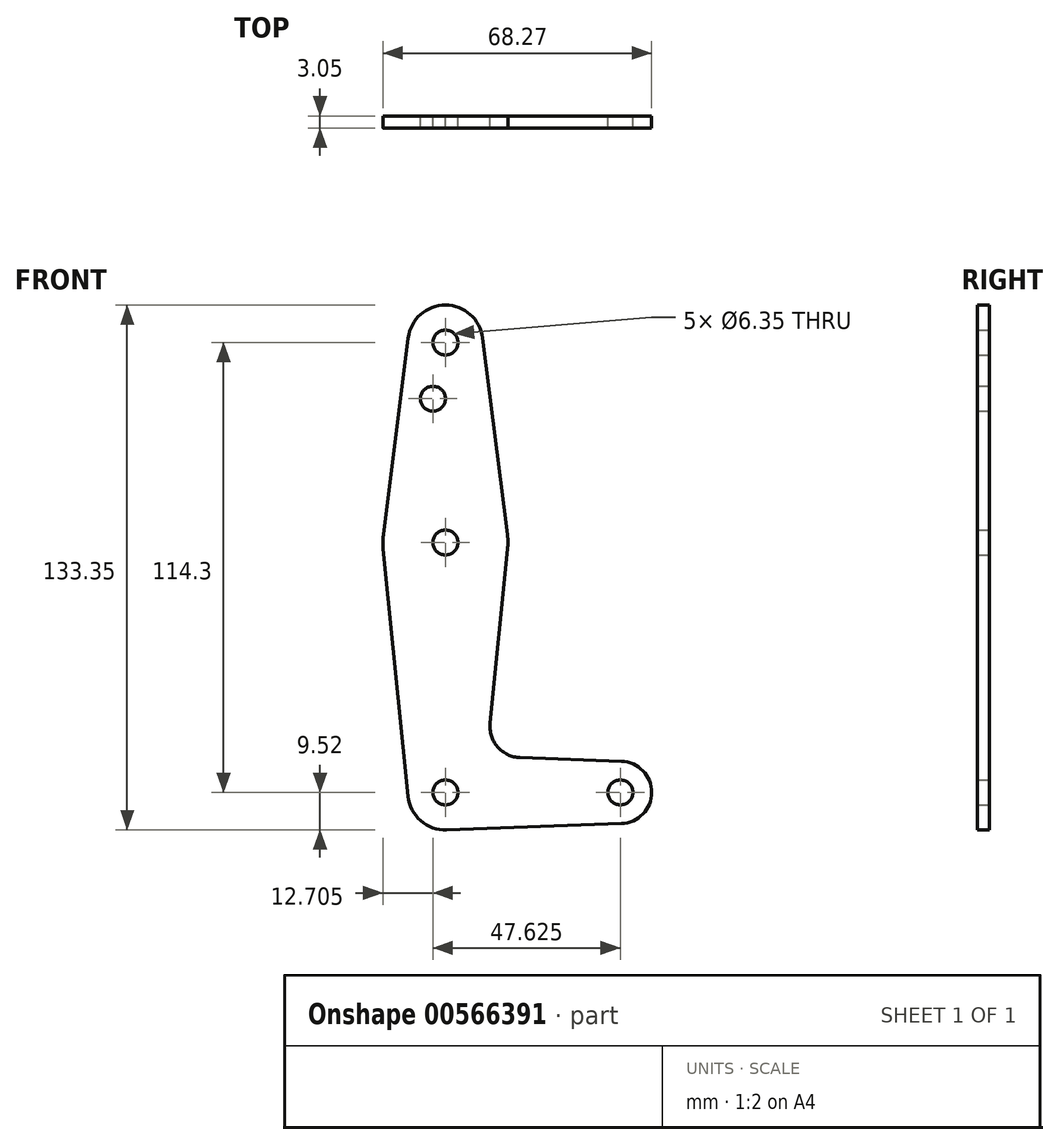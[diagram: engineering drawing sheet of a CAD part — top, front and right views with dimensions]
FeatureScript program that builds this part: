
annotation { "Feature Type Name" : "Feature", "Feature Type Description" : "" }
export const myFeature = defineFeature(function(context is Context, id is Id, definition is map)
    precondition{}
    {
        {
            var Q0;
            Q0=qCreatedBy(makeId("Front.planeOp"),FACE);
            var sketch = newSketch(context, id + "F0", { "sketchPlane" : qUnion([Q0])});
            skLineSegment(sketch, "E0", {"start": v(0, 114.3) * mm, "end": v(0, 0) * mm, "construction": true});
            skLineSegment(sketch, "E1", {"start": v(0, 0) * mm, "end": v(44.45, 0) * mm, "construction": true});
            skCircle(sketch, "E2", {"center": v(0, 114.3) * mm, "radius": 9.53 * mm});
            skCircle(sketch, "E3", {"center": v(0, 63.5) * mm, "radius": 15.88 * mm});
            skCircle(sketch, "E4", {"center": v(0, 0) * mm, "radius": 9.53 * mm});
            skCircle(sketch, "E5", {"center": v(44.45, 0) * mm, "radius": 7.94 * mm});
            skLineSegment(sketch, "E6", {"start": v(-15.8, 61.91) * mm, "end": v(-9.48, -0.95) * mm});
            skLineSegment(sketch, "E7", {"start": v(15.8, 61.91) * mm, "end": v(11.34, 17.6) * mm});
            skLineSegment(sketch, "E8", {"start": v(0.34, -9.52) * mm, "end": v(44.73, -7.93) * mm});
            skLineSegment(sketch, "E9", {"start": v(18.97, 8.85) * mm, "end": v(44.73, 7.93) * mm});
            skLineSegment(sketch, "E10", {"start": v(-9.45, 115.5) * mm, "end": v(-15.75, 65.48) * mm});
            skLineSegment(sketch, "E11", {"start": v(9.45, 115.5) * mm, "end": v(15.75, 65.48) * mm});
            skCircle(sketch, "E12", {"center": v(0, 114.3) * mm, "radius": 3.18 * mm});
            skCircle(sketch, "E13", {"center": v(0, 63.5) * mm, "radius": 3.18 * mm});
            skCircle(sketch, "E14", {"center": v(0, 0) * mm, "radius": 3.18 * mm});
            skCircle(sketch, "E15", {"center": v(44.45, 0) * mm, "radius": 3.18 * mm});
            skCircle(sketch, "E16", {"center": v(-3.17, 100.03) * mm, "radius": 3.18 * mm});
            skArc(sketch, "E17.filletArc", {"start": v(11.34, 17.6) * mm, "mid": v(13.26, 11.57) * mm, "end": v(18.97, 8.85) * mm});
            skSolve(sketch);
        }
        {
            var Q0;
            Q0 = qSketchRegion(id + "F0", true);
            extrude(context, id + "F1", {"entities" : qUnion([Q0]), "depth" : 3.05 * mm, "offsetDistance" : 25.4 * mm});
        }
    });
